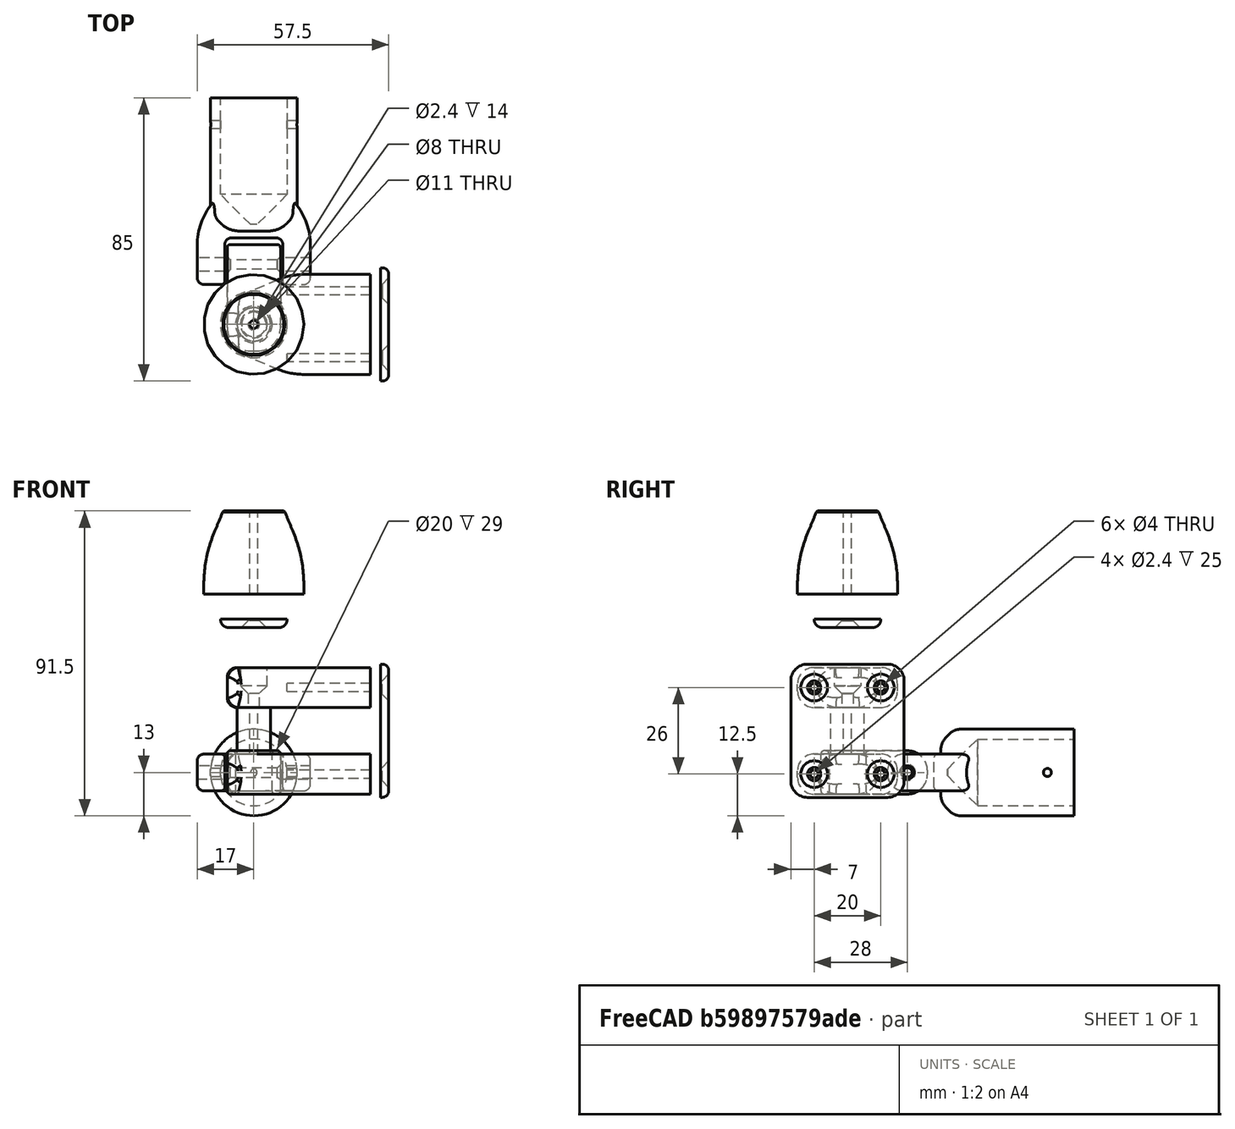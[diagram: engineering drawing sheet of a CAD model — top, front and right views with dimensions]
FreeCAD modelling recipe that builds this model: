
FCSTD DOCUMENT  (FreeCAD 1.0R38641 +678 (Git))
Label: LaundryBox
License: All rights reserved
LicenseURL: https://en.wikipedia.org/wiki/All_rights_reserved
objects: Part::Fillet×20, Part::Cylinder×14, Part::Chamfer×11, Part::MultiFuse×7, Part::Box×5, Part::Cut×5, Part::FeaturePython×3, Part::Feature×1
note: 66 computed .brp shape members not serialized (recipe doc carries the construction recipe); baked Part::Feature solids carry a one-line shape summary decoded from their .brp

FEATURE [Part::FeaturePython] Tube  # WARN: FeaturePython — macro-defined, semantics opaque (R4)
  AttacherType = Attacher::AttachEngine3D
  Height = 25
  InnerRadius = 1.2
  OuterRadius = 15
FEATURE [Part::Chamfer] Chamfer
  Base = -> Tube
  EdgeLinks = -> Tube [Edge1]
  Edges = 1 edges r=6: [Edge1]
FEATURE [Part::Chamfer] Chamfer001
  Base = -> Chamfer
  EdgeLinks = -> Chamfer [Edge2]
  Edges = 1 edges r=8: [Edge2]
FEATURE [Part::Fillet] Fillet  label="Distancer"
  Base = -> Chamfer001
  EdgeLinks = -> Chamfer001 [Edge2]
  Edges = 1 edges r=40: [Edge2]
  Placement = pos=(0,0,60) rot=(0,0,1;0rad)
FEATURE [Part::FeaturePython] Tube001  # WARN: FeaturePython — macro-defined, semantics opaque (R4)
  AttacherType = Attacher::AttachEngine3D
  Height = 2.5
  InnerRadius = 1.7
  OuterRadius = 10
FEATURE [Part::Chamfer] Chamfer002
  Base = -> Tube001
  EdgeLinks = -> Tube001 [Edge5]
  Edges = 1 edges r=2: [Edge5]
FEATURE [Part::Fillet] Fillet001  label="Cap"
  Base = -> Chamfer002
  EdgeLinks = -> Chamfer002 [Edge2]
  Edges = 1 edges r=2.4: [Edge2]
  Placement = pos=(0,0,50) rot=(0,0,1;0rad)
FEATURE [Part::FeaturePython] Tube002  # WARN: FeaturePython — macro-defined, semantics opaque (R4)
  AttacherType = Attacher::AttachEngine3D
  Height = 16
  InnerRadius = 1.2
  OuterRadius = 5
  Placement = pos=(0,0,10) rot=(0,0,1;0rad)
FEATURE [Part::Box] Box  label="Cube"
  AttacherType = Attacher::AttachEngine3D
  Height = 12
  Length = 43
  Placement = pos=(-8,-15,0) rot=(0,0,1;0rad)
  Width = 30
FEATURE [Part::Chamfer] Chamfer003
  Base = -> Box
  EdgeLinks = -> Box [Edge1,Edge3]
  Edges = 2 edges r=10: [Edge1,Edge3]
FEATURE [Part::Fillet] Fillet002
  Base = -> Chamfer003
  EdgeLinks = -> Chamfer003 [Edge2,Edge3]
  Edges = 2 edges r=10: [Edge2,Edge3]
FEATURE [Part::Chamfer] Chamfer004
  Base = -> Fillet002
  EdgeLinks = -> Fillet002 [Edge21,Edge22]
  Edges = 2 edges r=9: [Edge21,Edge22]
FEATURE [Part::Fillet] Fillet003
  Base = -> Chamfer004
  EdgeLinks = -> Chamfer004 [Edge15,Edge27]
  Edges = 2 edges r=20: [Edge15,Edge27]
FEATURE [Part::Fillet] Fillet004
  Base = -> Fillet003
  EdgeLinks = -> Fillet003 [Edge4,Edge8,Edge20,Edge28]
  Edges = 4 edges r=5: [Edge4,Edge8,Edge20,Edge28]
FEATURE [Part::Fillet] Fillet005
  Base = -> Fillet004
  EdgeLinks = -> Fillet004 [Edge26]
  Edges = 1 edges r=3: [Edge26]
FEATURE [Part::Cylinder] Cylinder  label="ScrewHolle001"
  Angle = 360
  AttacherType = Attacher::AttachEngine3D
  FirstAngle = 0
  Height = 30
  Placement = pos=(10,10,6) rot=(0,1,0;1.5708rad)
  Radius = 1.2
  SecondAngle = 0
FEATURE [Part::Cylinder] Cylinder001  label="ScrewHolle002"
  Angle = 360
  AttacherType = Attacher::AttachEngine3D
  FirstAngle = 0
  Height = 30
  Placement = pos=(10,-10,6) rot=(0,1,0;1.5708rad)
  Radius = 1.2
  SecondAngle = 0
FEATURE [Part::MultiFuse] Fusion
  Shapes = -> [Cylinder,Cylinder001]
FEATURE [Part::Cut] Cut
  Base = -> Fillet005
  Tool = -> Fusion
FEATURE [Part::Feature] Cut001  label="HindgeBody"
  Placement = pos=(0,0,26) rot=(0,0,1;0rad)
  shape: bbox 43.01 x 33.3 x 12 mm, 50 faces (baked)
FEATURE [Part::MultiFuse] Fusion001  label="Hindge001"
  Shapes = -> [Cut,Tube002]
FEATURE [Part::Cylinder] Cylinder002  label="ScrewHolle003"
  Angle = 360
  AttacherType = Attacher::AttachEngine3D
  FirstAngle = 0
  Height = 20
  Placement = pos=(0,0,24) rot=(0,0,1;0rad)
  Radius = 1.7
  SecondAngle = 0
FEATURE [Part::Cylinder] Cylinder003  label="ScrewHolle004"
  Angle = 360
  AttacherType = Attacher::AttachEngine3D
  FirstAngle = 0
  Height = 20
  Placement = pos=(0,0,30) rot=(0,0,1;0rad)
  Radius = 4
  SecondAngle = 0
FEATURE [Part::Chamfer] Chamfer005
  Base = -> Cylinder003
  EdgeLinks = -> Cylinder003 [Edge2]
  Edges = 1 edges r=2.5: [Edge2]
FEATURE [Part::MultiFuse] Fusion002
  Shapes = -> [Chamfer005,Cylinder002]
FEATURE [Part::Cut] Cut002  label="Hindge002"
  Base = -> Cut001
  Tool = -> Fusion002
FEATURE [Part::Cylinder] Cylinder004  label="ScrewHolle005"
  Angle = 360
  AttacherType = Attacher::AttachEngine3D
  FirstAngle = 0
  Height = 30
  Placement = pos=(20,10,32) rot=(0,1,0;1.5708rad)
  Radius = 2
  SecondAngle = 0
FEATURE [Part::Cylinder] Cylinder005  label="ScrewHolle006"
  Angle = 360
  AttacherType = Attacher::AttachEngine3D
  FirstAngle = 0
  Height = 30
  Placement = pos=(20,-10,6) rot=(0,1,0;1.5708rad)
  Radius = 2
  SecondAngle = 0
FEATURE [Part::Cylinder] Cylinder006  label="ScrewHolle007"
  Angle = 360
  AttacherType = Attacher::AttachEngine3D
  FirstAngle = 0
  Height = 30
  Placement = pos=(20,-10,32) rot=(0,1,0;1.5708rad)
  Radius = 2
  SecondAngle = 0
FEATURE [Part::Cylinder] Cylinder007  label="ScrewHolle008"
  Angle = 360
  AttacherType = Attacher::AttachEngine3D
  FirstAngle = 0
  Height = 30
  Placement = pos=(20,10,6) rot=(0,1,0;1.5708rad)
  Radius = 2
  SecondAngle = 0
FEATURE [Part::MultiFuse] Fusion003  label="CapScrewHolles"
  Shapes = -> [Cylinder004,Cylinder005,Cylinder006,Cylinder007]
FEATURE [Part::Box] Box001  label="Cube001"
  AttacherType = Attacher::AttachEngine3D
  Height = 40
  Length = 2.5
  Placement = pos=(38,-17,-1) rot=(0,0,1;0rad)
  Width = 34
FEATURE [Part::Fillet] Fillet006
  Base = -> Box001
  EdgeLinks = -> Box001 [Edge9,Edge10,Edge11,Edge12]
  Edges = 4 edges r=5: [Edge9,Edge10,Edge11,Edge12]
FEATURE [Part::Cut] Cut003
  Base = -> Fillet006
  Tool = -> Fusion003
FEATURE [Part::Chamfer] Chamfer006
  Base = -> Cut003
  EdgeLinks = -> Cut003 [Edge30,Edge32,Edge34,Edge36]
  Edges = 4 edges r=2: [Edge30,Edge32,Edge34,Edge36]
FEATURE [Part::Fillet] Fillet007  label="HindgeCap"
  Base = -> Chamfer006
  EdgeLinks = -> Chamfer006 [Edge17]
  Edges = 1 edges r=2: [Edge17]
FEATURE [Part::Cylinder] Cylinder008  label="Cylinder"
  Angle = 360
  AttacherType = Attacher::AttachEngine3D
  FirstAngle = 0
  Height = 20
  Radius = 5.5
  SecondAngle = 0
FEATURE [Part::Box] Box002  label="Cube002"
  AttacherType = Attacher::AttachEngine3D
  Height = 13
  Length = 16
  Placement = pos=(-8,-8,0) rot=(0,0,1;0rad)
  Width = 32
FEATURE [Part::Fillet] Fillet008
  Base = -> Box002
  EdgeLinks = -> Box002 [Edge1,Edge5]
  Edges = 2 edges r=7: [Edge1,Edge5]
FEATURE [Part::Fillet] Fillet009
  Base = -> Fillet008
  EdgeLinks = -> Fillet008 [Edge6,Edge12]
  Edges = 2 edges r=6: [Edge6,Edge12]
FEATURE [Part::Fillet] Fillet010
  Base = -> Fillet009
  EdgeLinks = -> Fillet009 [Edge9]
  Edges = 1 edges r=1: [Edge9]
FEATURE [Part::Cylinder] Cylinder009
  Angle = 360
  AttacherType = Attacher::AttachEngine3D
  FirstAngle = 0
  Height = 20
  Placement = pos=(-10,18,6.5) rot=(0,1,0;1.5708rad)
  Radius = 1.4
  SecondAngle = 0
FEATURE [Part::MultiFuse] Fusion004
  Shapes = -> [Cylinder009,Cylinder008]
FEATURE [Part::Cut] Cut004
  Base = -> Fillet010
  Tool = -> Fusion004
FEATURE [Part::Fillet] Fillet011
  Base = -> Cut004
  EdgeLinks = -> Cut004 [Edge35,Edge40]
  Edges = 2 edges r=1: [Edge35,Edge40]
FEATURE [Part::Chamfer] Chamfer007  label="Hindge003"
  Base = -> Fillet011
  EdgeLinks = -> Fillet011 [Edge37,Edge42]
  Edges = 2 edges r=1: [Edge37,Edge42]
FEATURE [Part::Box] Box003  label="Cube003"
  AttacherType = Attacher::AttachEngine3D
  Height = 13
  Length = 17.4
  Placement = pos=(-8.7,0,0) rot=(0,0,1;0rad)
  Width = 26
FEATURE [Part::Fillet] Fillet012
  Base = -> Box003
  EdgeLinks = -> Box003 [Edge3,Edge7]
  Edges = 2 edges r=2: [Edge3,Edge7]
FEATURE [Part::Box] Box004  label="Cube004"
  AttacherType = Attacher::AttachEngine3D
  Height = 11
  Length = 34
  Placement = pos=(-17,12,1) rot=(0,0,1;0rad)
  Width = 30
FEATURE [Part::Fillet] Fillet013
  Base = -> Box004
  EdgeLinks = -> Box004 [Edge9,Edge10]
  Edges = 2 edges r=5: [Edge9,Edge10]
FEATURE [Part::Cylinder] Cylinder010
  Angle = 360
  AttacherType = Attacher::AttachEngine3D
  FirstAngle = 0
  Height = 50
  Placement = pos=(-25,18,6.5) rot=(0,1,0;1.5708rad)
  Radius = 2
  SecondAngle = 0
FEATURE [Part::Cylinder] Cylinder011
  Angle = 360
  AttacherType = Attacher::AttachEngine3D
  FirstAngle = 0
  Height = 40
  Placement = pos=(0,70,6.5) rot=(1,0,0;1.5708rad)
  Radius = 10
  SecondAngle = 0
FEATURE [Part::Chamfer] Chamfer008
  Base = -> Cylinder011
  EdgeLinks = -> Cylinder011 [Edge3]
  Edges = 1 edges r=9: [Edge3]
FEATURE [Part::Cylinder] Cylinder012
  Angle = 360
  AttacherType = Attacher::AttachEngine3D
  FirstAngle = 0
  Height = 40
  Placement = pos=(0,68,6.5) rot=(1,0,0;1.5708rad)
  Radius = 13
  SecondAngle = 0
FEATURE [Part::Chamfer] Chamfer009
  Base = -> Cylinder012
  EdgeLinks = -> Cylinder012 [Edge3]
  Edges = 1 edges r=4: [Edge3]
FEATURE [Part::Fillet] Fillet016
  Base = -> Chamfer009
  EdgeLinks = -> Chamfer009 [Edge5]
  Edges = 1 edges r=6: [Edge5]
FEATURE [Part::Fillet] Fillet017
  Base = -> Fillet016
  EdgeLinks = -> Fillet016 [Edge3]
  Edges = 1 edges r=5: [Edge3]
FEATURE [Part::Cylinder] Cylinder013
  Angle = 360
  AttacherType = Attacher::AttachEngine3D
  FirstAngle = 0
  Height = 30
  Placement = pos=(-15,60,6.5) rot=(0,1,0;1.5708rad)
  Radius = 1.2
  SecondAngle = 0
FEATURE [Part::Chamfer] Chamfer010
  Base = -> Fillet013
  EdgeLinks = -> Fillet013 [Edge6,Edge18]
  Edges = 2 edges r=10: [Edge6,Edge18]
FEATURE [Part::Fillet] Fillet018
  Base = -> Chamfer010
  EdgeLinks = -> Chamfer010 [Edge2,Edge24]
  Edges = 2 edges r=20: [Edge2,Edge24]
FEATURE [Part::Fillet] Fillet019
  Base = -> Fillet018
  EdgeLinks = -> Fillet018 [Edge22]
  Edges = 1 edges r=2: [Edge22]
FEATURE [Part::Fillet] Fillet020
  Base = -> Fillet019
  EdgeLinks = -> Fillet019 [Edge22]
  Edges = 1 edges r=2: [Edge22]
FEATURE [Part::MultiFuse] Fusion005
  Shapes = -> [Chamfer008,Cylinder013,Cylinder010,Fillet012]
FEATURE [Part::MultiFuse] Fusion006
  Shapes = -> [Fillet020,Fillet017]
FEATURE [Part::Cut] Cut005
  Base = -> Fusion006
  Tool = -> Fusion005
FEATURE [Part::Fillet] Fillet021  label="Hindge004"
  Base = -> Cut005
  EdgeLinks = -> Cut005 [Edge43]
  Edges = 1 edges r=1: [Edge43]
